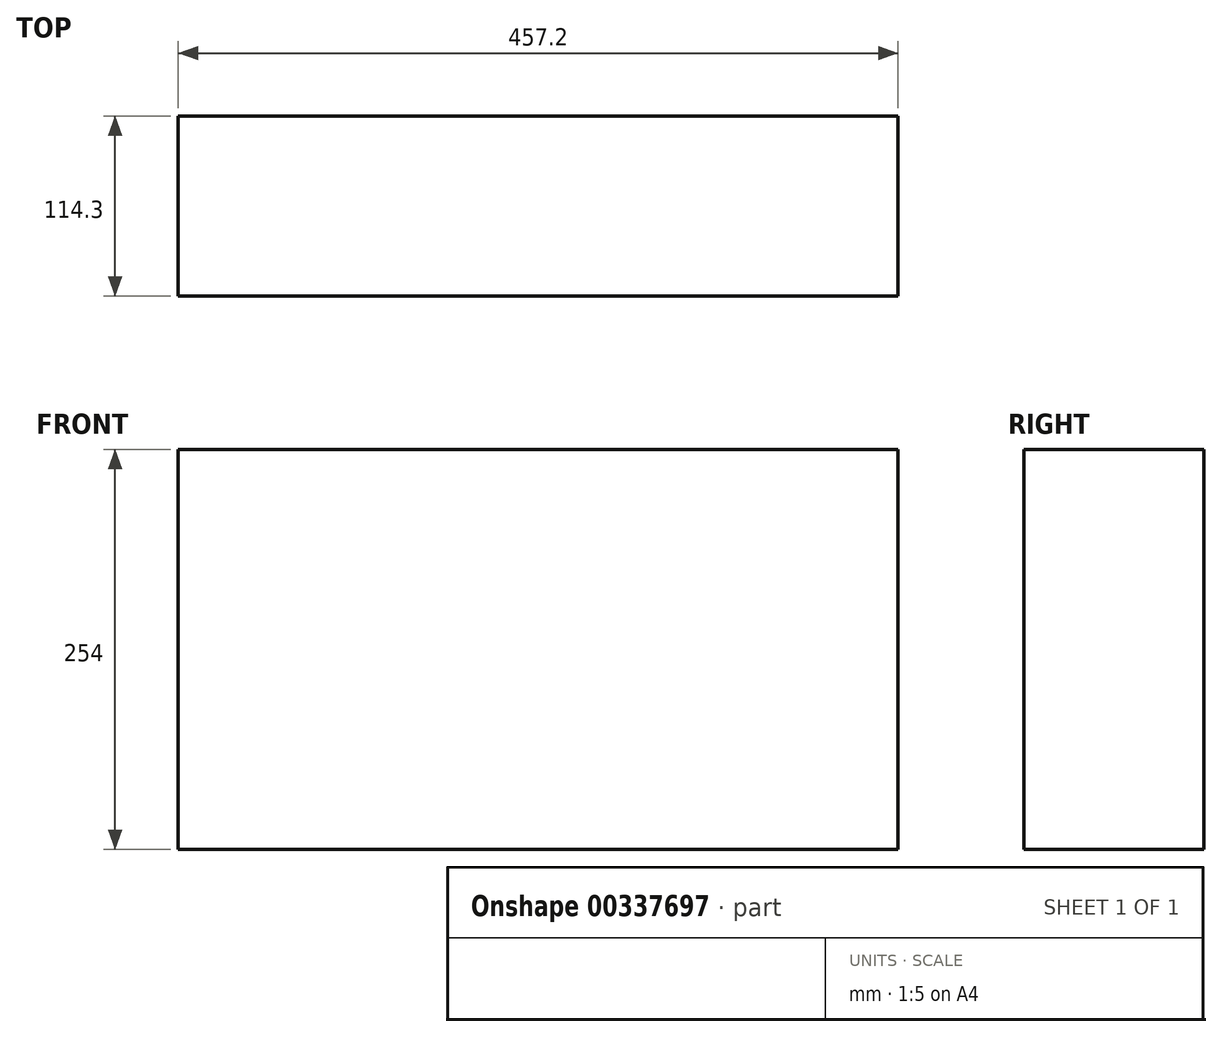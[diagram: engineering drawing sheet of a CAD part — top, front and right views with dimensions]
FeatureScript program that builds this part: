
annotation { "Feature Type Name" : "Feature", "Feature Type Description" : "" }
export const myFeature = defineFeature(function(context is Context, id is Id, definition is map)
    precondition{}
    {
        {
            var Q0;
            Q0=qCreatedBy(makeId("Front.planeOp"),FACE);
            var sketch = newSketch(context, id + "F0", { "sketchPlane" : qUnion([Q0])});
            skLineSegment(sketch, "E0.bottom", {"start": v(0, 0) * mm, "end": v(457.2, 0) * mm});
            skLineSegment(sketch, "E0.top", {"start": v(0, 254) * mm, "end": v(457.2, 254) * mm});
            skLineSegment(sketch, "E0.left", {"start": v(0, 0) * mm, "end": v(0, 254) * mm});
            skLineSegment(sketch, "E0.right", {"start": v(457.2, 0) * mm, "end": v(457.2, 254) * mm});
            skSolve(sketch);
        }
        {
            var Q0;
            Q0 = qSketchRegion(id + "F0", true);
            extrude(context, id + "F1", {"entities" : qUnion([Q0]), "depth" : 114.3 * mm});
        }
    });
